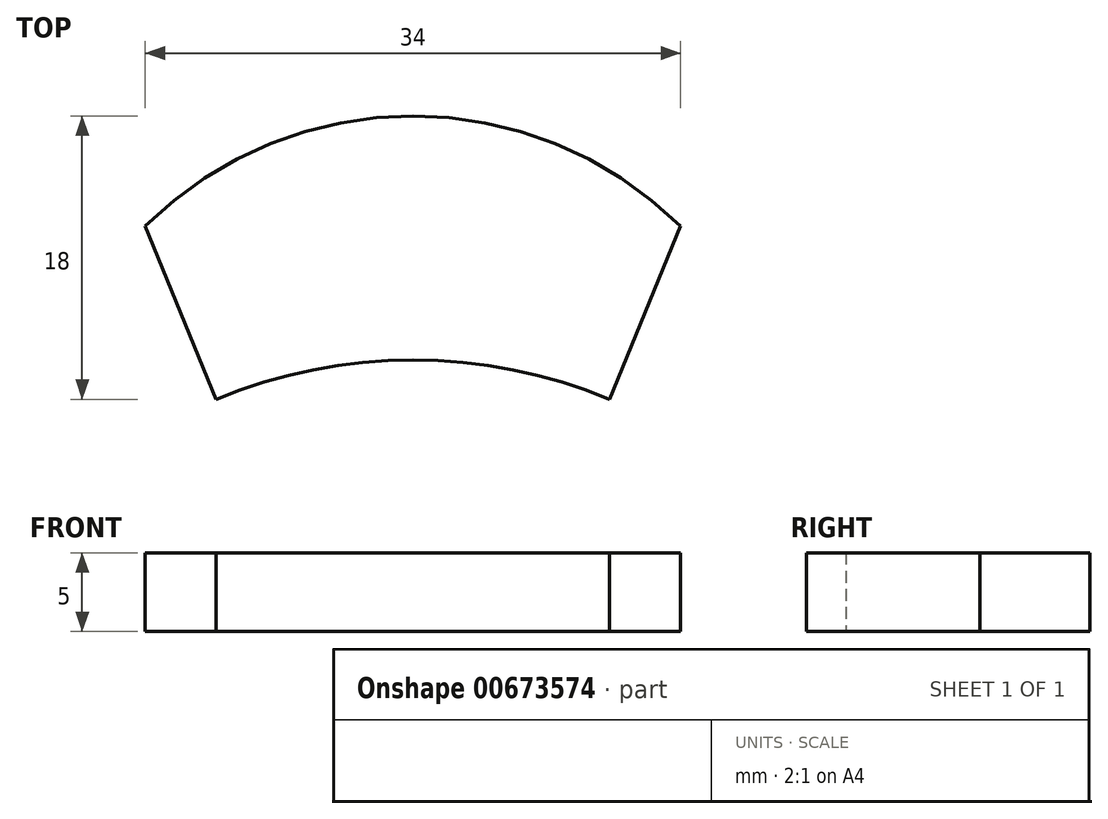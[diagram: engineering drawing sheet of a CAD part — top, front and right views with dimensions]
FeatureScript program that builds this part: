
annotation { "Feature Type Name" : "Feature", "Feature Type Description" : "" }
export const myFeature = defineFeature(function(context is Context, id is Id, definition is map)
    precondition{}
    {
        {
            var Q0;
            Q0=qCreatedBy(makeId("Top.planeOp"),FACE);
            var sketch = newSketch(context, id + "F0", { "sketchPlane" : qUnion([Q0])});
            skLineSegment(sketch, "E0", {"start": v(0, 0) * mm, "end": v(-25, 0) * mm});
            skLineSegment(sketch, "E1", {"start": v(-12.5, 0) * mm, "end": v(-12.5, 11) * mm});
            skLineSegment(sketch, "E2", {"start": v(-12.5, 11) * mm, "end": v(-29.5, 11) * mm});
            skLineSegment(sketch, "E3", {"start": v(-25, 0) * mm, "end": v(-29.5, 11) * mm});
            skLineSegment(sketch, "E4.MirrorCS", {"start": v(0, 0) * mm, "end": v(4.5, 11) * mm});
            skArc(sketch, "E5", {"start": v(0, 0) * mm, "mid": v(-12.5, 2.5) * mm, "end": v(-25, 0) * mm});
            skArc(sketch, "E6", {"start": v(4.5, 11) * mm, "mid": v(-12.5, 18) * mm, "end": v(-29.5, 11) * mm});
            skSolve(sketch);
        }
        {
            var Q0;
            {var subQ0=sQuery(id+"F0.wireOp",EDGE,"E2");Q0=makeQuery(id+"F0.imprint","IMPRINT",FACE,{"disambiguationData":[TD([[makeQuery(id+"F0.imprint","IMPRINT",EDGE,{"derivedFrom":subQ0}),1.0]])]});}
            var Q1;
            {var subQ4=sQuery(id+"F0.wireOp",EDGE,"E2");Q1=makeQuery(id+"F0.imprint","IMPRINT",FACE,{"disambiguationData":[TD([[makeQuery(id+"F0.imprint","IMPRINT",EDGE,{"derivedFrom":subQ4}),-1.0]])]});}
            extrude(context, id + "F1", {"entities" : qUnion([Q0, Q1]), "depth" : 5 * mm, "offsetDistance" : 25 * mm});
        }
    });
